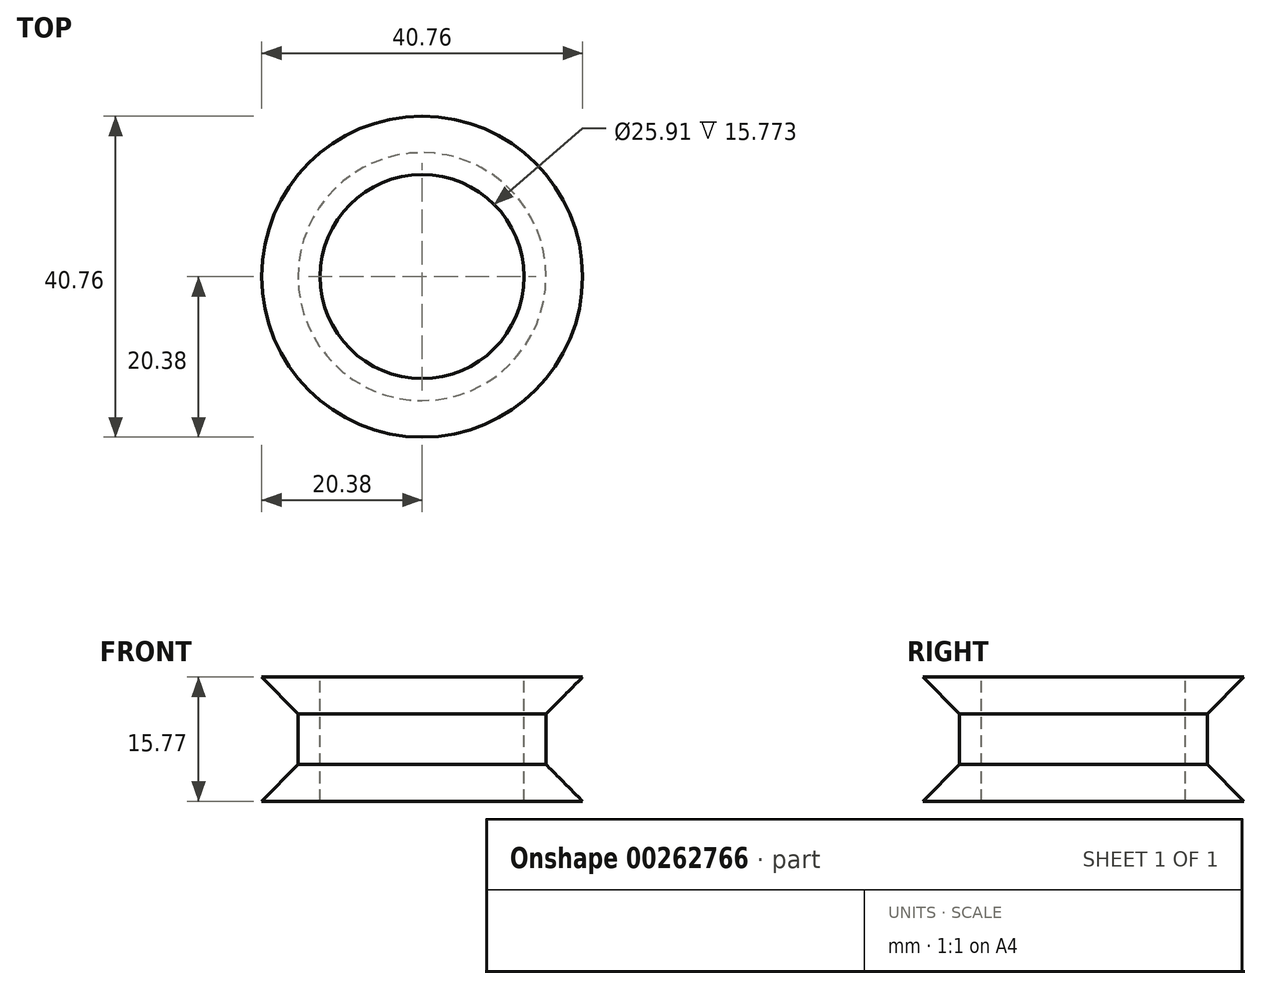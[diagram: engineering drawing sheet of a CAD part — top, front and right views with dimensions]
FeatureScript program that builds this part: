
annotation { "Feature Type Name" : "Feature", "Feature Type Description" : "" }
export const myFeature = defineFeature(function(context is Context, id is Id, definition is map)
    precondition{}
    {
        {
            var Q0;
            Q0=qCreatedBy(makeId("Top.planeOp"),FACE);
            var sketch = newSketch(context, id + "F0", { "sketchPlane" : qUnion([Q0])});
            skCircle(sketch, "E0", {"center": v(0, 0) * mm, "radius": 20.38 * mm});
            skSolve(sketch);
        }
        {
            var Q0;
            Q0=makeQuery(id+"F0.imprint","IMPRINT",FACE,{"disambiguationData":[TD([[makeQuery(id+"F0.imprint","IMPRINT",EDGE,{"derivedFrom":sQuery(id+"F0.wireOp",EDGE,"E0")}),1.0]])]});
            cPlane(context, id + "F1", {"entities" : qUnion([Q0]), "cplaneType" : CPlaneType.OFFSET, "offset" : 4.67 * mm, "width" : 152.4 * mm, "height" : 152.4 * mm});
        }
        {
            var Q0;
            Q0=qCreatedBy(id+"F1.planeOp",FACE);
            var sketch = newSketch(context, id + "F2", { "sketchPlane" : qUnion([Q0])});
            skCircle(sketch, "E1", {"center": v(0, 0) * mm, "radius": 15.75 * mm});
            skSolve(sketch);
        }
        {
            var Q0;
            Q0=makeQuery(id+"F0.imprint","IMPRINT",FACE,{"disambiguationData":[TD([[makeQuery(id+"F0.imprint","IMPRINT",EDGE,{"derivedFrom":sQuery(id+"F0.wireOp",EDGE,"E0")}),1.0]])]});
            var Q1;
            Q1=makeQuery(id+"F2.imprint","IMPRINT",FACE,{"disambiguationData":[TD([[makeQuery(id+"F2.imprint","IMPRINT",EDGE,{"derivedFrom":sQuery(id+"F2.wireOp",EDGE,"E1")}),1.0]])]});
            loft(context, id + "F3", {"sheetProfilesArray" : [{ "sheetProfileEntities" : qUnion([Q0]) }, { "sheetProfileEntities" : qUnion([Q1]) }]});
        }
        {
            var Q0;
            Q0=makeQuery(id+"F3.opLoft","CAP_FACE",FACE,{"disambiguationData":[OSD([makeQuery(id+"F2.imprint","IMPRINT",FACE,{"disambiguationData":[TD([[makeQuery(id+"F2.imprint","IMPRINT",EDGE,{"derivedFrom":sQuery(id+"F2.wireOp",EDGE,"E1")}),1.0]])]})])],"isStart":true});
            extrude(context, id + "F4", {"entities" : qUnion([Q0]), "operationType" : NewBodyOperationType.ADD, "depth" : 6.43 * mm});
        }
        {
            var Q0;
            Q0=makeQuery(id+"F4.opExtrude","CAP_FACE",FACE,{"disambiguationData":[OSD([makeQuery(id+"F2.imprint","IMPRINT",FACE,{"disambiguationData":[TD([[makeQuery(id+"F2.imprint","IMPRINT",EDGE,{"derivedFrom":sQuery(id+"F2.wireOp",EDGE,"E1")}),1.0]])]})])],"isStart":false});
            cPlane(context, id + "F5", {"entities" : qUnion([Q0]), "cplaneType" : CPlaneType.OFFSET, "offset" : 4.67 * mm, "width" : 152.4 * mm, "height" : 152.4 * mm});
        }
        {
            var Q0;
            Q0=qCreatedBy(id+"F5.planeOp",FACE);
            var sketch = newSketch(context, id + "F6", { "sketchPlane" : qUnion([Q0])});
            skCircle(sketch, "E2", {"center": v(0, 0) * mm, "radius": 20.38 * mm});
            skSolve(sketch);
        }
        {
            var Q1;
            Q1=makeQuery(id+"F6.imprint","IMPRINT",FACE,{"disambiguationData":[TD([[makeQuery(id+"F6.imprint","IMPRINT",EDGE,{"derivedFrom":sQuery(id+"F6.wireOp",EDGE,"E2")}),1.0]])]});
            var Q2;
            Q2=makeQuery(id+"F4.opExtrude","CAP_FACE",FACE,{"disambiguationData":[OSD([makeQuery(id+"F2.imprint","IMPRINT",FACE,{"disambiguationData":[TD([[makeQuery(id+"F2.imprint","IMPRINT",EDGE,{"derivedFrom":sQuery(id+"F2.wireOp",EDGE,"E1")}),1.0]])]})])],"isStart":false});
            loft(context, id + "F7", {"operationType" : NewBodyOperationType.ADD, "sheetProfilesArray" : [{ "sheetProfileEntities" : qUnion([Q1]) }, { "sheetProfileEntities" : qUnion([Q2]) }]});
        }
        {
            var Q0;
            Q0=qCreatedBy(id+"F5.planeOp",FACE);
            var sketch = newSketch(context, id + "F8", { "sketchPlane" : qUnion([Q0])});
            skPoint(sketch, "E3", {"position": v(0, 0) * mm});
            skSolve(sketch);
        }
        {
            var Q0;
            Q0=sQuery(id+"F8.wireOp",VERTEX,"E3");
            var Q1;
            Q1=makeQuery(id+"F3.opLoft","SWEPT_BODY",BODY,{"disambiguationData":[OSD([makeQuery(id+"F0.imprint","IMPRINT",FACE,{"disambiguationData":[TD([[makeQuery(id+"F0.imprint","IMPRINT",EDGE,{"derivedFrom":sQuery(id+"F0.wireOp",EDGE,"E0")}),1.0]])]}),makeQuery(id+"F2.imprint","IMPRINT",FACE,{"disambiguationData":[TD([[makeQuery(id+"F2.imprint","IMPRINT",EDGE,{"derivedFrom":sQuery(id+"F2.wireOp",EDGE,"E1")}),1.0]])]})])]});
            hole(context, id + "F9", {"style" : HoleStyle.SIMPLE, "endStyle" : HoleEndStyle.THROUGH, "holeDiameter" : 25.9 * mm, "tappedDepth" : 12.7 * mm, "tapClearance" : 3, "locations" : qUnion([Q0]), "scope" : qUnion([Q1])});
        }
    });
